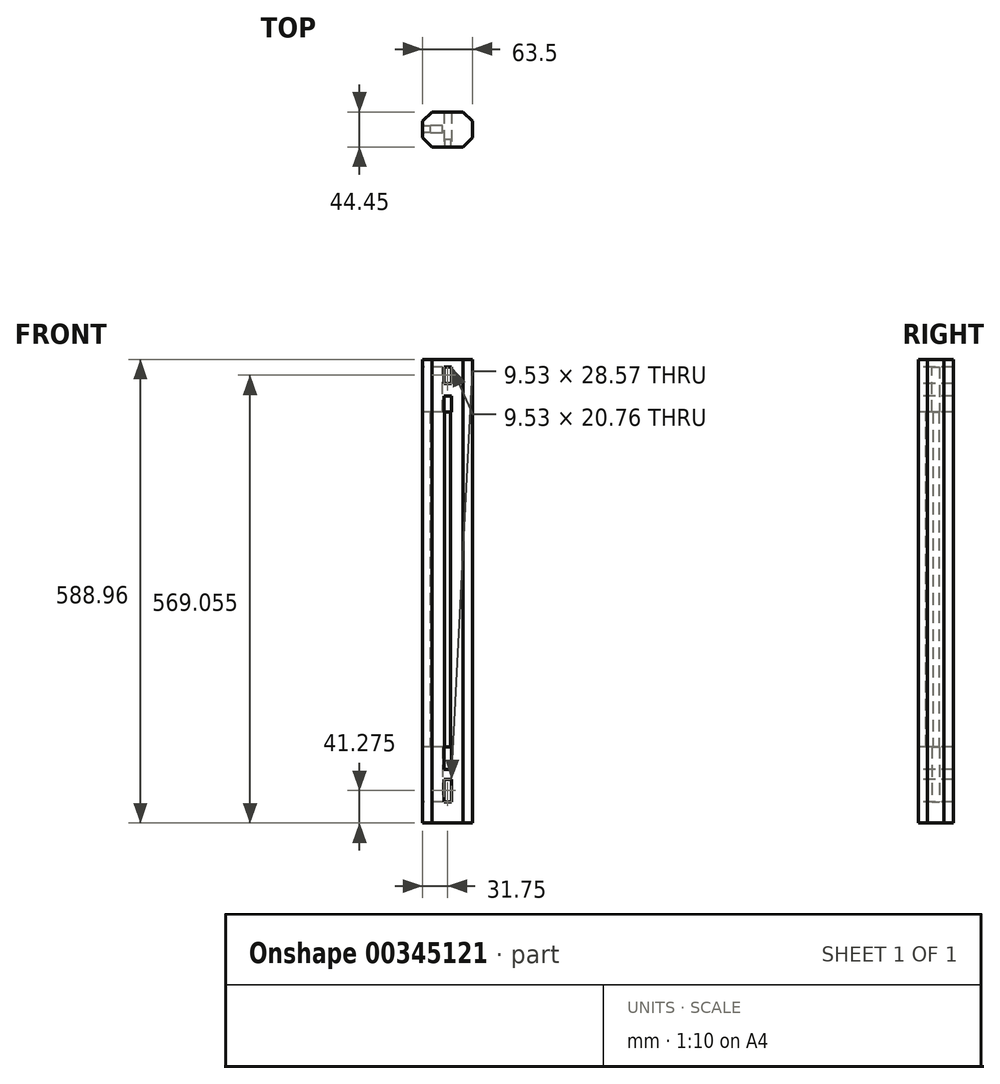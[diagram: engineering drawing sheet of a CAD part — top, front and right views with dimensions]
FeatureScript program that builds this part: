
annotation { "Feature Type Name" : "Feature", "Feature Type Description" : "" }
export const myFeature = defineFeature(function(context is Context, id is Id, definition is map)
    precondition{}
    {
        {
            var Q0;
            Q0=qCreatedBy(makeId("Top.planeOp"),FACE);
            var sketch = newSketch(context, id + "F0", { "sketchPlane" : qUnion([Q0])});
            skLineSegment(sketch, "E0", {"start": v(0, 0) * mm, "end": v(63.5, 0) * mm});
            skLineSegment(sketch, "E1", {"start": v(63.5, 0) * mm, "end": v(63.5, 44.45) * mm});
            skLineSegment(sketch, "E2", {"start": v(63.5, 44.45) * mm, "end": v(0, 44.45) * mm});
            skLineSegment(sketch, "E3", {"start": v(0, 44.45) * mm, "end": v(0, 0) * mm});
            skSolve(sketch);
        }
        {
            var Q0;
            Q0=qSketchRegion(id+"F0",true);
            extrude(context, id + "F1", {"entities" : qUnion([Q0]), "depth" : 588.96 * mm});
        }
        {
            var Q0;
            Q0=makeQuery(id+"F1.opExtrude","SWEPT_FACE",FACE,{"disambiguationData":[OSD([sQuery(id+"F0.wireOp",EDGE,"E3")])]});
            var sketch = newSketch(context, id + "F2", { "sketchPlane" : qUnion([Q0])});
            skLineSegment(sketch, "E4", {"start": v(-26.99, 579.44) * mm, "end": v(-26.99, 522.29) * mm});
            skLineSegment(sketch, "E5", {"start": v(-26.99, 522.29) * mm, "end": v(-17.46, 522.29) * mm});
            skLineSegment(sketch, "E6", {"start": v(-17.46, 522.29) * mm, "end": v(-17.46, 579.44) * mm});
            skLineSegment(sketch, "E7", {"start": v(-17.46, 579.44) * mm, "end": v(-26.99, 579.44) * mm});
            skPoint(sketch, "E8", {"position": v(-26.2, 522.29) * mm});
            skPoint(sketch, "E9", {"position": v(-18.26, 522.29) * mm});
            skLineSegment(sketch, "E10.bottom", {"start": v(-17.46, 96.84) * mm, "end": v(-26.99, 96.84) * mm});
            skLineSegment(sketch, "E10.top", {"start": v(-17.46, 26.99) * mm, "end": v(-26.99, 26.99) * mm});
            skLineSegment(sketch, "E10.left", {"start": v(-17.46, 96.84) * mm, "end": v(-17.46, 26.99) * mm});
            skLineSegment(sketch, "E10.right", {"start": v(-26.99, 96.84) * mm, "end": v(-26.99, 26.99) * mm});
            skPoint(sketch, "E10.middle", {"position": v(-22.23, 61.91) * mm});
            skPoint(sketch, "E10.middle.positionSnap0", {"position": v(-22.22, 0) * mm});
            skPoint(sketch, "E10.centerSnap0", {"position": v(-22.22, 0) * mm});
            skLineSegment(sketch, "E11", {"start": v(-18.26, 522.29) * mm, "end": v(-18.26, 96.84) * mm});
            skLineSegment(sketch, "E12", {"start": v(-26.2, 522.29) * mm, "end": v(-26.2, 96.84) * mm});
            skSolve(sketch);
        }
        {
            var Q0;
            {var subQ4=sQuery(id+"F2.wireOp",EDGE,"E4");Q0=makeQuery(id+"F2.imprint","IMPRINT",FACE,{"disambiguationData":[TD([[makeQuery(id+"F2.imprint","IMPRINT",EDGE,{"derivedFrom":subQ4}),1.0]])]});}
            var Q1;
            Q1=makeQuery(id+"F2.imprint","IMPRINT",FACE,{"disambiguationData":[TD([[makeQuery(id+"F2.imprint","IMPRINT",EDGE,{"derivedFrom":sQuery(id+"F2.wireOp",EDGE,"E10.top")}),-1.0]])]});
            extrude(context, id + "F3", {"entities" : qUnion([Q0, Q1]), "operationType" : NewBodyOperationType.REMOVE, "oppositeDirection" : true, "depth" : 25.4 * mm});
        }
        {
            var Q0;
            Q0=qSketchRegion(id+"F2",true);
            extrude(context, id + "F4", {"entities" : qUnion([Q0]), "operationType" : NewBodyOperationType.REMOVE, "oppositeDirection" : true, "depth" : 9.52 * mm});
        }
        {
            var Q0;
            Q0=makeQuery(id+"F1.opExtrude","SWEPT_FACE",FACE,{"disambiguationData":[OSD([sQuery(id+"F0.wireOp",EDGE,"E0")])]});
            var sketch = newSketch(context, id + "F5", { "sketchPlane" : qUnion([Q0])});
            skLineSegment(sketch, "E13", {"start": v(26.99, 579.44) * mm, "end": v(26.99, 558.67) * mm});
            skLineSegment(sketch, "E14", {"start": v(26.99, 558.67) * mm, "end": v(36.51, 558.67) * mm});
            skLineSegment(sketch, "E15", {"start": v(36.51, 558.67) * mm, "end": v(36.51, 579.44) * mm});
            skLineSegment(sketch, "E16", {"start": v(36.51, 579.44) * mm, "end": v(26.99, 579.44) * mm});
            skPoint(sketch, "E17.startSnap0", {"position": v(26.99, 569.06) * mm});
            skLineSegment(sketch, "E18", {"start": v(26.99, 55.56) * mm, "end": v(36.51, 55.56) * mm});
            skLineSegment(sketch, "E19", {"start": v(28.78, 522.03) * mm, "end": v(26.99, 522.03) * mm});
            skLineSegment(sketch, "E20", {"start": v(26.99, 522.03) * mm, "end": v(26.99, 522.03) * mm});
            skLineSegment(sketch, "E21", {"start": v(26.99, 522.03) * mm, "end": v(26.99, 542.8) * mm});
            skLineSegment(sketch, "E22", {"start": v(26.99, 542.8) * mm, "end": v(36.51, 542.8) * mm});
            skLineSegment(sketch, "E23", {"start": v(36.51, 542.8) * mm, "end": v(36.51, 522.03) * mm});
            skLineSegment(sketch, "E24", {"start": v(36.51, 522.03) * mm, "end": v(28.78, 522.03) * mm});
            skLineSegment(sketch, "E25", {"start": v(26.99, 55.56) * mm, "end": v(26.99, 55.56) * mm});
            skLineSegment(sketch, "E26", {"start": v(26.99, 55.56) * mm, "end": v(26.99, 26.99) * mm});
            skLineSegment(sketch, "E27", {"start": v(36.51, 55.56) * mm, "end": v(36.51, 26.99) * mm});
            skLineSegment(sketch, "E28", {"start": v(36.51, 26.99) * mm, "end": v(26.99, 26.99) * mm});
            skLineSegment(sketch, "E29", {"start": v(36.51, 68.26) * mm, "end": v(36.51, 96.84) * mm});
            skLineSegment(sketch, "E30", {"start": v(36.51, 96.84) * mm, "end": v(26.99, 96.84) * mm});
            skLineSegment(sketch, "E31", {"start": v(26.99, 96.84) * mm, "end": v(26.99, 68.26) * mm});
            skLineSegment(sketch, "E32", {"start": v(26.99, 68.26) * mm, "end": v(36.51, 68.26) * mm});
            skPoint(sketch, "E33", {"position": v(35.82, 96.84) * mm});
            skPoint(sketch, "E34", {"position": v(27.88, 96.84) * mm});
            skLineSegment(sketch, "E35", {"start": v(35.82, 96.84) * mm, "end": v(35.82, 522.03) * mm});
            skLineSegment(sketch, "E36", {"start": v(27.88, 96.84) * mm, "end": v(27.88, 522.03) * mm});
            skSolve(sketch);
        }
        {
            var Q0;
            {var subQ0=sQuery(id+"F5.wireOp",EDGE,"E35");Q0=makeQuery(id+"F5.imprint","IMPRINT",FACE,{"disambiguationData":[TD([[makeQuery(id+"F5.imprint","IMPRINT",EDGE,{"derivedFrom":subQ0}),1.0]])]});}
            extrude(context, id + "F6", {"entities" : qUnion([Q0]), "operationType" : NewBodyOperationType.REMOVE, "oppositeDirection" : true, "depth" : 9.52 * mm});
        }
        {
            var Q0;
            Q0=makeQuery(id+"F5.imprint","IMPRINT",FACE,{"disambiguationData":[TD([[makeQuery(id+"F5.imprint","IMPRINT",EDGE,{"derivedFrom":sQuery(id+"F5.wireOp",EDGE,"E13")}),1.0]])]});
            var Q1;
            {var subQ0=sQuery(id+"F5.wireOp",EDGE,"E21");Q1=makeQuery(id+"F5.imprint","IMPRINT",FACE,{"disambiguationData":[TD([[makeQuery(id+"F5.imprint","IMPRINT",EDGE,{"derivedFrom":subQ0}),-1.0]])]});}
            var Q2;
            {var subQ4=sQuery(id+"F5.wireOp",EDGE,"E29");Q2=makeQuery(id+"F5.imprint","IMPRINT",FACE,{"disambiguationData":[TD([[makeQuery(id+"F5.imprint","IMPRINT",EDGE,{"derivedFrom":subQ4}),1.0]])]});}
            var Q3;
            Q3=makeQuery(id+"F5.imprint","IMPRINT",FACE,{"disambiguationData":[TD([[makeQuery(id+"F5.imprint","IMPRINT",EDGE,{"derivedFrom":sQuery(id+"F5.wireOp",EDGE,"E18")}),-1.0]])]});
            extrude(context, id + "F7", {"entities" : qUnion([Q0, Q1, Q2, Q3]), "operationType" : NewBodyOperationType.REMOVE, "endBound" : BoundingType.THROUGH_ALL, "oppositeDirection" : true, "depth" : 25.4 * mm});
        }
        {
            var Q0;
            Q0=makeQuery(id+"F1.opExtrude","SWEPT_EDGE",EDGE,{"disambiguationData":[OSD([sQuery(id+"F0.wireOp",EDGE,"E1"),sQuery(id+"F0.wireOp",EDGE,"E2")])]});
            var Q1;
            Q1=makeQuery(id+"F1.opExtrude","SWEPT_EDGE",EDGE,{"disambiguationData":[OSD([sQuery(id+"F0.wireOp",EDGE,"E2"),sQuery(id+"F0.wireOp",EDGE,"E3")])]});
            var Q2;
            Q2=makeQuery(id+"F1.opExtrude","SWEPT_EDGE",EDGE,{"disambiguationData":[OSD([sQuery(id+"F0.wireOp",EDGE,"E0"),sQuery(id+"F0.wireOp",EDGE,"E1")])]});
            var Q3;
            Q3=makeQuery(id+"F1.opExtrude","SWEPT_EDGE",EDGE,{"disambiguationData":[OSD([sQuery(id+"F0.wireOp",EDGE,"E0"),sQuery(id+"F0.wireOp",EDGE,"E3")])]});
            chamfer(context, id + "F8", {"entities" : qUnion([Q0, Q1, Q2, Q3]), "width" : 11.9 * mm, "tangentPropagation" : true});
        }
    });
